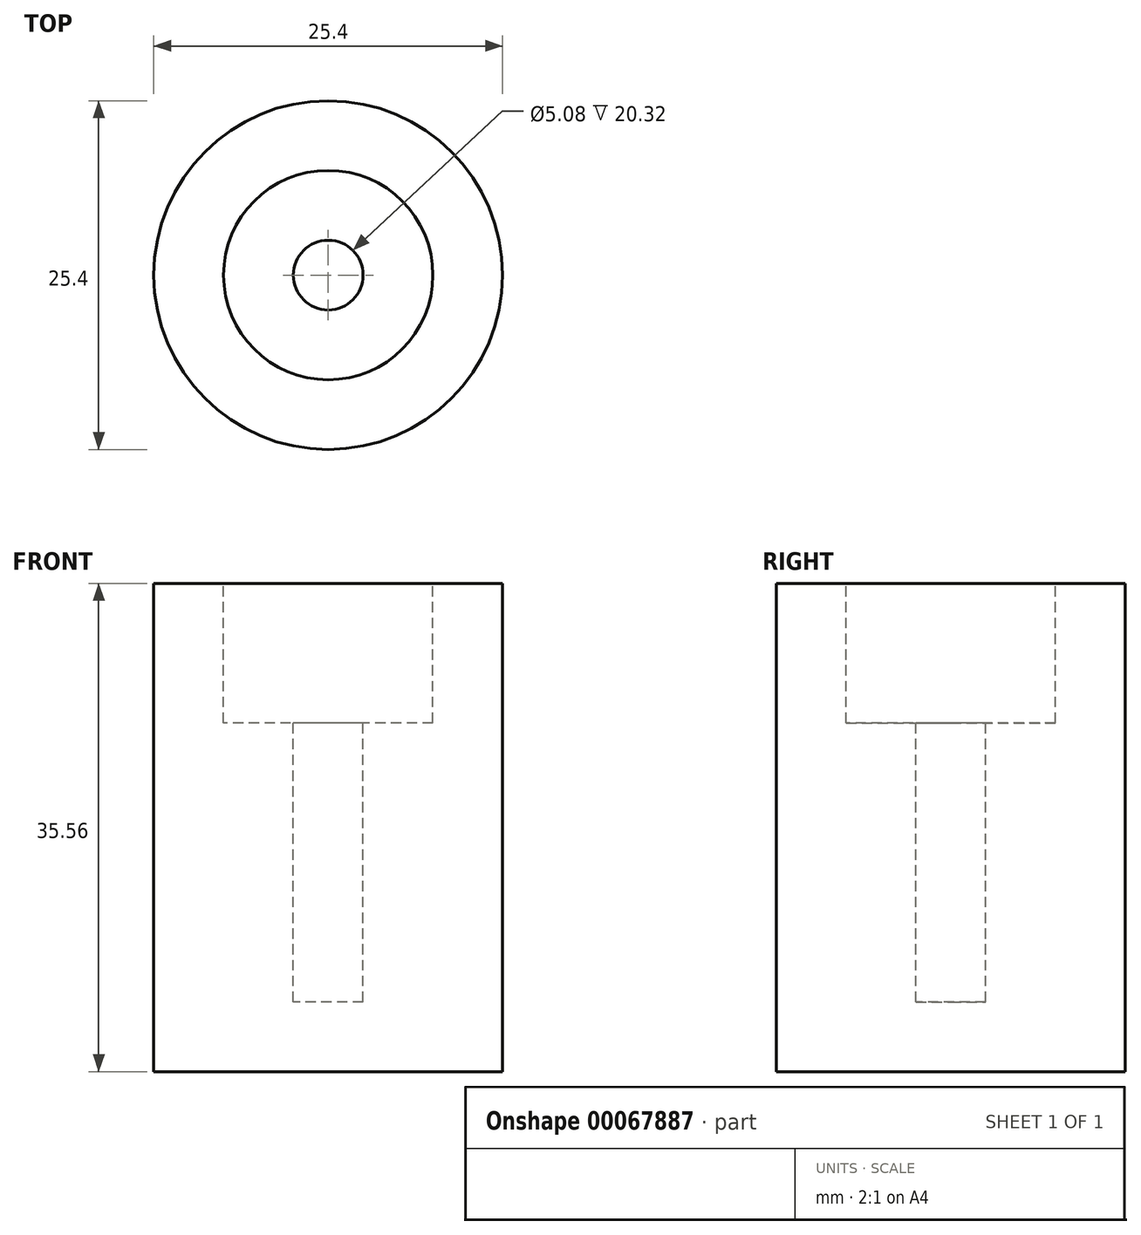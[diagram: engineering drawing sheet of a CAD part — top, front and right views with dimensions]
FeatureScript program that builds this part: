
annotation { "Feature Type Name" : "Feature", "Feature Type Description" : "" }
export const myFeature = defineFeature(function(context is Context, id is Id, definition is map)
    precondition{}
    {
        {
            var Q0;
            Q0=qCreatedBy(makeId("Top.planeOp"),FACE);
            var sketch = newSketch(context, id + "F0", { "sketchPlane" : qUnion([Q0])});
            skCircle(sketch, "E0", {"center": v(0, 0) * mm, "radius": 12.7 * mm});
            skSolve(sketch);
        }
        {
            var Q0;
            Q0=makeQuery(id+"F0.imprint","IMPRINT",FACE,{"disambiguationData":[TD([[makeQuery(id+"F0.imprint","IMPRINT",EDGE,{"derivedFrom":sQuery(id+"F0.wireOp",EDGE,"E0")}),1.0]])]});
            extrude(context, id + "F1", {"entities" : qUnion([Q0]), "depth" : 35.56 * mm});
        }
        {
            var Q0;
            Q0=makeQuery(id+"F1.opExtrude","CAP_FACE",FACE,{"disambiguationData":[OSD([sQuery(id+"F0.wireOp",EDGE,"E0")])],"isStart":false});
            var sketch = newSketch(context, id + "F2", { "sketchPlane" : qUnion([Q0])});
            skCircle(sketch, "E1", {"center": v(0, 0) * mm, "radius": 7.62 * mm});
            skCircle(sketch, "E2", {"center": v(0, 0) * mm, "radius": 2.54 * mm});
            skSolve(sketch);
        }
        {
            var Q0;
            Q0=makeQuery(id+"F2.imprint","IMPRINT",FACE,{"disambiguationData":[TD([[makeQuery(id+"F2.imprint","IMPRINT",EDGE,{"derivedFrom":sQuery(id+"F2.wireOp",EDGE,"E1")}),1.0]])]});
            extrude(context, id + "F3", {"entities" : qUnion([Q0]), "operationType" : NewBodyOperationType.REMOVE, "oppositeDirection" : true, "depth" : 10.16 * mm});
        }
        {
            var Q0;
            Q0=makeQuery(id+"F3.boolean.opBoolean","SPLIT",FACE,{"disambiguationData":[TD([makeQuery(id+"F3.opExtrude","SWEPT_FACE",FACE,{"disambiguationData":[OSD([sQuery(id+"F2.wireOp",EDGE,"E2")])]})])],"derivedFrom":makeQuery(id+"F1.opExtrude","CAP_FACE",FACE,{"disambiguationData":[OSD([sQuery(id+"F0.wireOp",EDGE,"E0")])],"isStart":false})});
            extrude(context, id + "F4", {"entities" : qUnion([Q0]), "operationType" : NewBodyOperationType.REMOVE, "oppositeDirection" : true, "depth" : 30.48 * mm});
        }
    });
